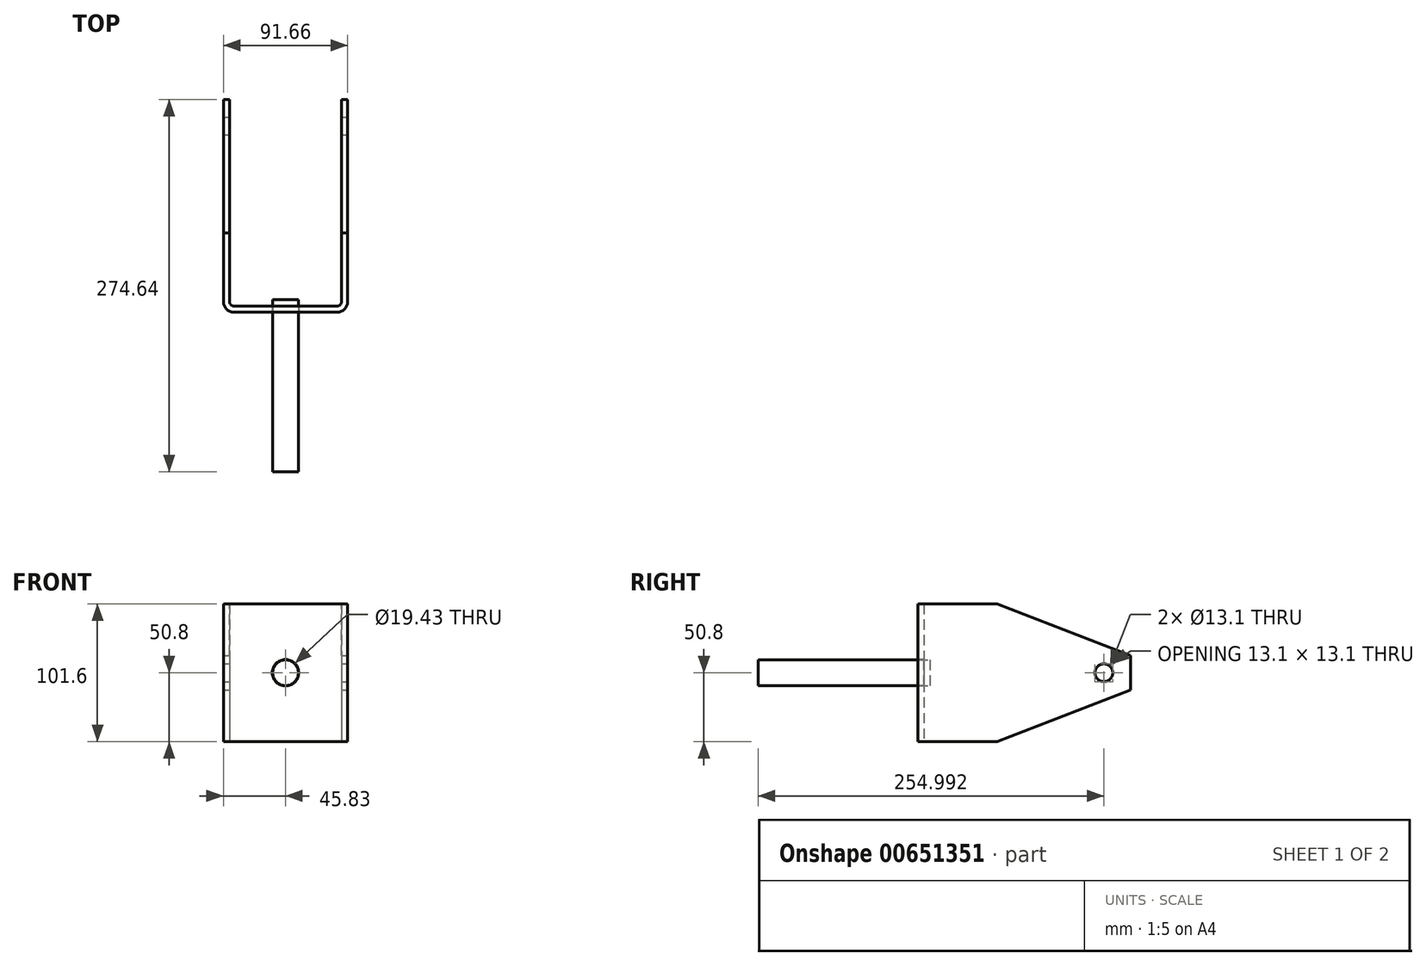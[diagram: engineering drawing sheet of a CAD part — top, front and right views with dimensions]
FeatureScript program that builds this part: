
annotation { "Feature Type Name" : "Feature", "Feature Type Description" : "" }
export const myFeature = defineFeature(function(context is Context, id is Id, definition is map)
    precondition{}
    {
        {
            var Q0;
            Q0=qCreatedBy(makeId("Front.planeOp"),FACE);
            var sketch = newSketch(context, id + "F0", { "sketchPlane" : qUnion([Q0])});
            skCircle(sketch, "E0", {"center": v(0, 0) * mm, "radius": 9.53 * mm});
            skSolve(sketch);
        }
        {
            var Q0;
            Q0 = qSketchRegion(id + "F0", true);
            extrude(context, id + "F1", {"entities" : qUnion([Q0]), "endBound" : BoundingType.SYMMETRIC, "depth" : 127 * mm, "offsetDistance" : 25.4 * mm});
        }
        {
            var Q0;
            Q0=qCreatedBy(makeId("Right.planeOp"),FACE);
            var sketch = newSketch(context, id + "F2", { "sketchPlane" : qUnion([Q0])});
            skLineSegment(sketch, "E1", {"start": v(58.74, 50.8) * mm, "end": v(58.74, -50.8) * mm});
            skLineSegment(sketch, "E2", {"start": v(58.74, -50.8) * mm, "end": v(54.18, -50.8) * mm});
            skLineSegment(sketch, "E3", {"start": v(54.18, -50.8) * mm, "end": v(54.18, 50.8) * mm});
            skLineSegment(sketch, "E4", {"start": v(54.18, 50.8) * mm, "end": v(58.74, 50.8) * mm});
            skSolve(sketch);
        }
        {
            var Q0;
            Q0 = qSketchRegion(id + "F2", true);
            extrude(context, id + "F3", {"entities" : qUnion([Q0]), "endBound" : BoundingType.SYMMETRIC, "depth" : 76.2 * mm, "offsetDistance" : 25.4 * mm});
        }
        {
            var Q0;
            Q0=qCreatedBy(makeId("Top.planeOp"),FACE);
            var sketch = newSketch(context, id + "F4", { "sketchPlane" : qUnion([Q0])});
            skLineSegment(sketch, "E5", {"start": v(41.27, 61.91) * mm, "end": v(41.27, 211.14) * mm});
            skArc(sketch, "E6", {"start": v(41.27, 61.91) * mm, "mid": v(40.35, 59.67) * mm, "end": v(38.1, 58.74) * mm});
            skLineSegment(sketch, "E7.0", {"start": v(38.1, 54.18) * mm, "end": v(38.1, 58.74) * mm});
            skLineSegment(sketch, "E8", {"start": v(41.27, 211.14) * mm, "end": v(45.83, 211.14) * mm});
            skLineSegment(sketch, "E9", {"start": v(45.83, 211.14) * mm, "end": v(45.83, 61.91) * mm});
            skArc(sketch, "E10", {"start": v(45.83, 61.91) * mm, "mid": v(43.57, 56.45) * mm, "end": v(38.1, 54.18) * mm});
            skLineSegment(sketch, "E11", {"start": v(0, 58.74) * mm, "end": v(0, 94.51) * mm, "construction": true});
            skLineSegment(sketch, "E12.MirrorCS", {"start": v(-41.27, 211.14) * mm, "end": v(-45.83, 211.14) * mm});
            skLineSegment(sketch, "E13.MirrorCS", {"start": v(-41.27, 61.91) * mm, "end": v(-41.27, 211.14) * mm});
            skArc(sketch, "E14.MirrorCS", {"start": v(-41.27, 61.91) * mm, "mid": v(-40.35, 59.67) * mm, "end": v(-38.1, 58.74) * mm});
            skLineSegment(sketch, "E15.MirrorCS", {"start": v(-38.1, 54.18) * mm, "end": v(-38.1, 58.74) * mm});
            skLineSegment(sketch, "E16.MirrorCS", {"start": v(-45.83, 211.14) * mm, "end": v(-45.83, 61.91) * mm});
            skArc(sketch, "E17.MirrorCS", {"start": v(-45.83, 61.91) * mm, "mid": v(-43.57, 56.45) * mm, "end": v(-38.1, 54.18) * mm});
            skSolve(sketch);
        }
        {
            var Q0;
            Q0 = qSketchRegion(id + "F4", true);
            extrude(context, id + "F5", {"entities" : qUnion([Q0]), "operationType" : NewBodyOperationType.ADD, "endBound" : BoundingType.SYMMETRIC, "depth" : 101.6 * mm, "offsetDistance" : 25.4 * mm});
        }
        {
            var Q0;
            Q0=makeQuery(id+"F5.opExtrude","SWEPT_FACE",FACE,{"disambiguationData":[OSD([sQuery(id+"F4.wireOp",EDGE,"E9")])]});
            var sketch = newSketch(context, id + "F6", { "sketchPlane" : qUnion([Q0])});
            skLineSegment(sketch, "E18.0", {"start": v(211.14, 50.8) * mm, "end": v(112.71, 50.8) * mm});
            skLineSegment(sketch, "E19.0", {"start": v(211.14, -50.8) * mm, "end": v(112.71, -50.8) * mm});
            skLineSegment(sketch, "E20.0", {"start": v(211.14, 50.8) * mm, "end": v(211.14, 12.7) * mm});
            skLineSegment(sketch, "E21", {"start": v(112.71, -50.8) * mm, "end": v(211.14, -12.7) * mm});
            skLineSegment(sketch, "E22", {"start": v(112.71, 50.8) * mm, "end": v(211.14, 12.7) * mm});
            skPoint(sketch, "E23.orphan", {"position": v(61.91, 50.8) * mm});
            skPoint(sketch, "E24.orphan", {"position": v(61.91, -50.8) * mm});
            skLineSegment(sketch, "E25.trimOffspring", {"start": v(211.14, -12.7) * mm, "end": v(211.14, -50.8) * mm});
            skCircle(sketch, "E26", {"center": v(191.5, 0) * mm, "radius": 6.55 * mm});
            skSolve(sketch);
        }
        {
            var Q0;
            Q0=makeQuery(id+"F6.imprint","IMPRINT",FACE,{"disambiguationData":[TD([[makeQuery(id+"F6.imprint","IMPRINT",EDGE,{"derivedFrom":sQuery(id+"F6.wireOp",EDGE,"E18.0")}),1.0]])]});
            var Q1;
            Q1=makeQuery(id+"F6.imprint","IMPRINT",FACE,{"disambiguationData":[TD([[makeQuery(id+"F6.imprint","IMPRINT",EDGE,{"derivedFrom":sQuery(id+"F6.wireOp",EDGE,"E19.0")}),-1.0]])]});
            var Q2;
            Q2=makeQuery(id+"F6.imprint","IMPRINT",FACE,{"disambiguationData":[TD([[makeQuery(id+"F6.imprint","IMPRINT",EDGE,{"derivedFrom":sQuery(id+"F6.wireOp",EDGE,"E26")}),1.0]])]});
            extrude(context, id + "F7", {"entities" : qUnion([Q0, Q1, Q2]), "operationType" : NewBodyOperationType.REMOVE, "endBound" : BoundingType.THROUGH_ALL, "oppositeDirection" : true, "depth" : 25.4 * mm, "offsetDistance" : 25.4 * mm});
        }
        {
            var Q0;
            Q0=makeQuery(id+"F3.opExtrude","SWEPT_FACE",FACE,{"disambiguationData":[OSD([sQuery(id+"F2.wireOp",EDGE,"E3")])]});
            var sketch = newSketch(context, id + "F8", { "sketchPlane" : qUnion([Q0])});
            skCircle(sketch, "E27", {"center": v(0, 0) * mm, "radius": 9.72 * mm});
            skCircle(sketch, "E28.0", {"center": v(0, 0) * mm, "radius": 9.53 * mm});
            skSolve(sketch);
        }
        {
            var Q0;
            Q0 = qSketchRegion(id + "F8", true);
            extrude(context, id + "F9", {"entities" : qUnion([Q0]), "operationType" : NewBodyOperationType.REMOVE, "endBound" : BoundingType.THROUGH_ALL, "oppositeDirection" : true, "depth" : 25.4 * mm, "offsetDistance" : 25.4 * mm});
        }
    });
